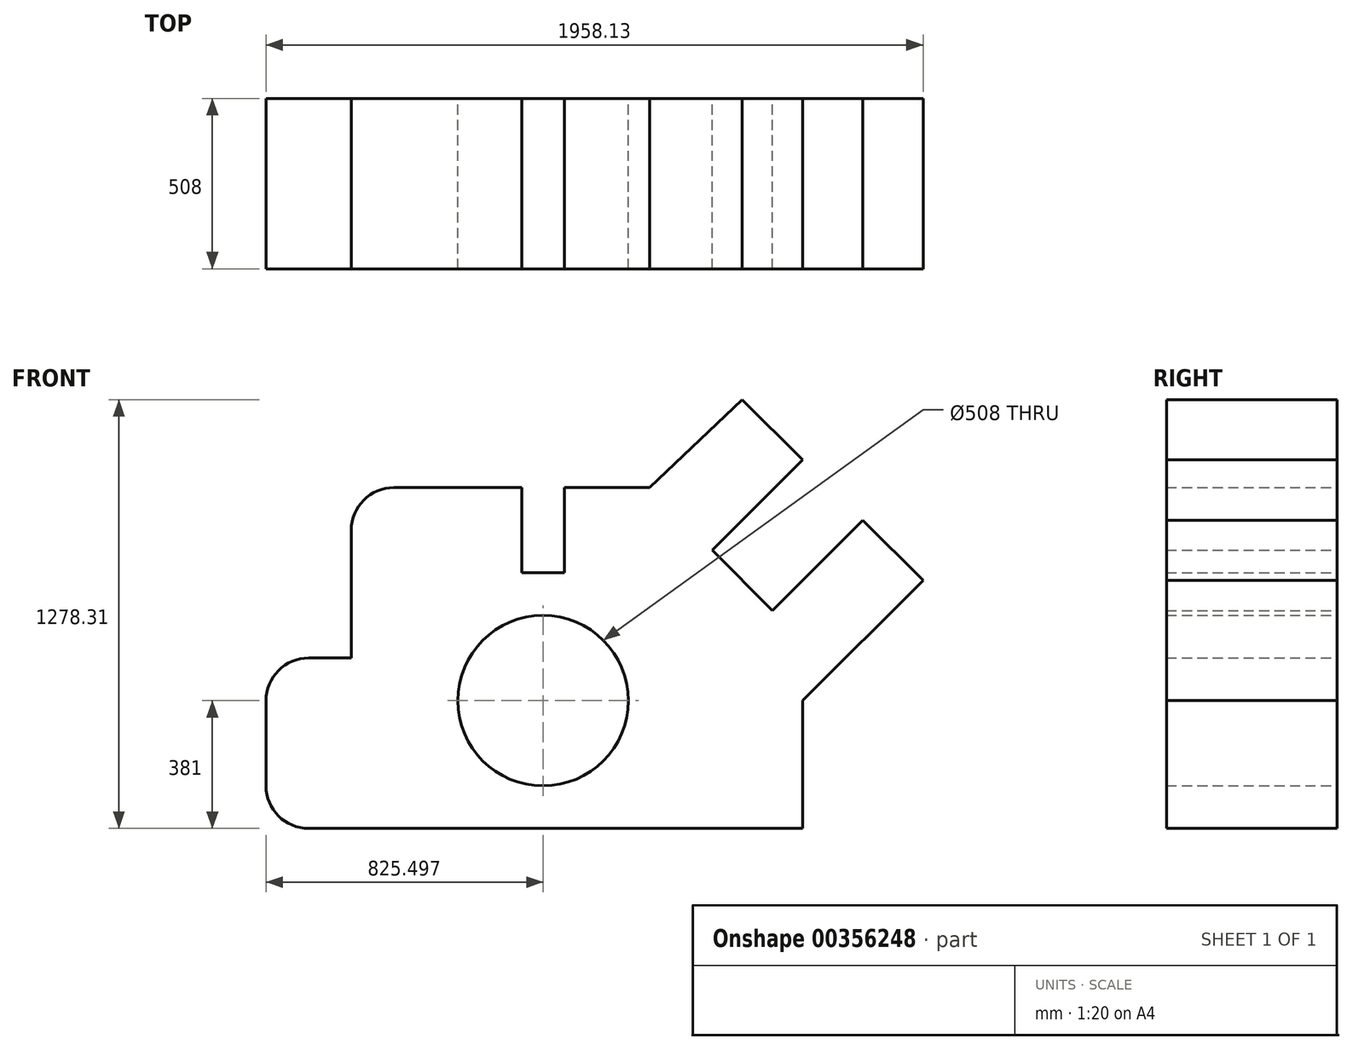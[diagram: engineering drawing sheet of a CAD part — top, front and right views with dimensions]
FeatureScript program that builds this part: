
annotation { "Feature Type Name" : "Feature", "Feature Type Description" : "" }
export const myFeature = defineFeature(function(context is Context, id is Id, definition is map)
    precondition{}
    {
        {
            var Q0;
            Q0=qCreatedBy(makeId("Front.planeOp"),FACE);
            var sketch = newSketch(context, id + "F0", { "sketchPlane" : qUnion([Q0])});
            skLineSegment(sketch, "E0", {"start": v(0, 0) * mm, "end": v(0, 381) * mm});
            skLineSegment(sketch, "E1", {"start": v(0, 0) * mm, "end": v(-1472.64, 0) * mm});
            skLineSegment(sketch, "E2", {"start": v(-1599.64, 127) * mm, "end": v(-1599.64, 381) * mm});
            skArc(sketch, "E3", {"start": v(-1599.64, 127) * mm, "mid": v(-1562.45, 37.2) * mm, "end": v(-1472.64, 0) * mm});
            skLineSegment(sketch, "E4", {"start": v(-1472.64, 508) * mm, "end": v(-1345.64, 508) * mm});
            skArc(sketch, "E5", {"start": v(-1472.64, 508) * mm, "mid": v(-1562.45, 470.8) * mm, "end": v(-1599.64, 381) * mm});
            skPoint(sketch, "E6.orphan", {"position": v(-1599.64, 508) * mm});
            skLineSegment(sketch, "E7", {"start": v(-1345.64, 508) * mm, "end": v(-1345.64, 889) * mm});
            skLineSegment(sketch, "E8", {"start": v(-1218.64, 1016) * mm, "end": v(-837.64, 1016) * mm});
            skArc(sketch, "E9", {"start": v(-1218.64, 1016) * mm, "mid": v(-1308.45, 978.8) * mm, "end": v(-1345.64, 889) * mm});
            skLineSegment(sketch, "E10", {"start": v(-837.64, 1016) * mm, "end": v(-837.64, 762) * mm});
            skLineSegment(sketch, "E11", {"start": v(-837.64, 762) * mm, "end": v(-710.64, 762) * mm});
            skLineSegment(sketch, "E12", {"start": v(-710.64, 762) * mm, "end": v(-710.64, 1016) * mm});
            skLineSegment(sketch, "E13", {"start": v(-710.64, 1016) * mm, "end": v(-456.64, 1016) * mm});
            skCircle(sketch, "E14", {"center": v(-774.14, 381) * mm, "radius": 254 * mm});
            skLineSegment(sketch, "E15", {"start": v(0, 381) * mm, "end": v(358.5, 739.5) * mm});
            skLineSegment(sketch, "E16", {"start": v(358.5, 739.5) * mm, "end": v(178.89, 919.1) * mm});
            skLineSegment(sketch, "E17", {"start": v(178.89, 919.1) * mm, "end": v(-90.52, 649.7) * mm});
            skLineSegment(sketch, "E18", {"start": v(-90.52, 649.7) * mm, "end": v(-270.12, 829.3) * mm});
            skLineSegment(sketch, "E19", {"start": v(-270.12, 829.3) * mm, "end": v(-0.72, 1098.7) * mm});
            skLineSegment(sketch, "E20", {"start": v(-0.72, 1098.7) * mm, "end": v(-180.32, 1278.31) * mm});
            skLineSegment(sketch, "E21", {"start": v(-180.32, 1278.31) * mm, "end": v(-456.64, 1016) * mm});
            skSolve(sketch);
        }
        {
            var Q0;
            Q0 = qSketchRegion(id + "F0", true);
            extrude(context, id + "F1", {"entities" : qUnion([Q0]), "depth" : 508 * mm});
        }
    });
